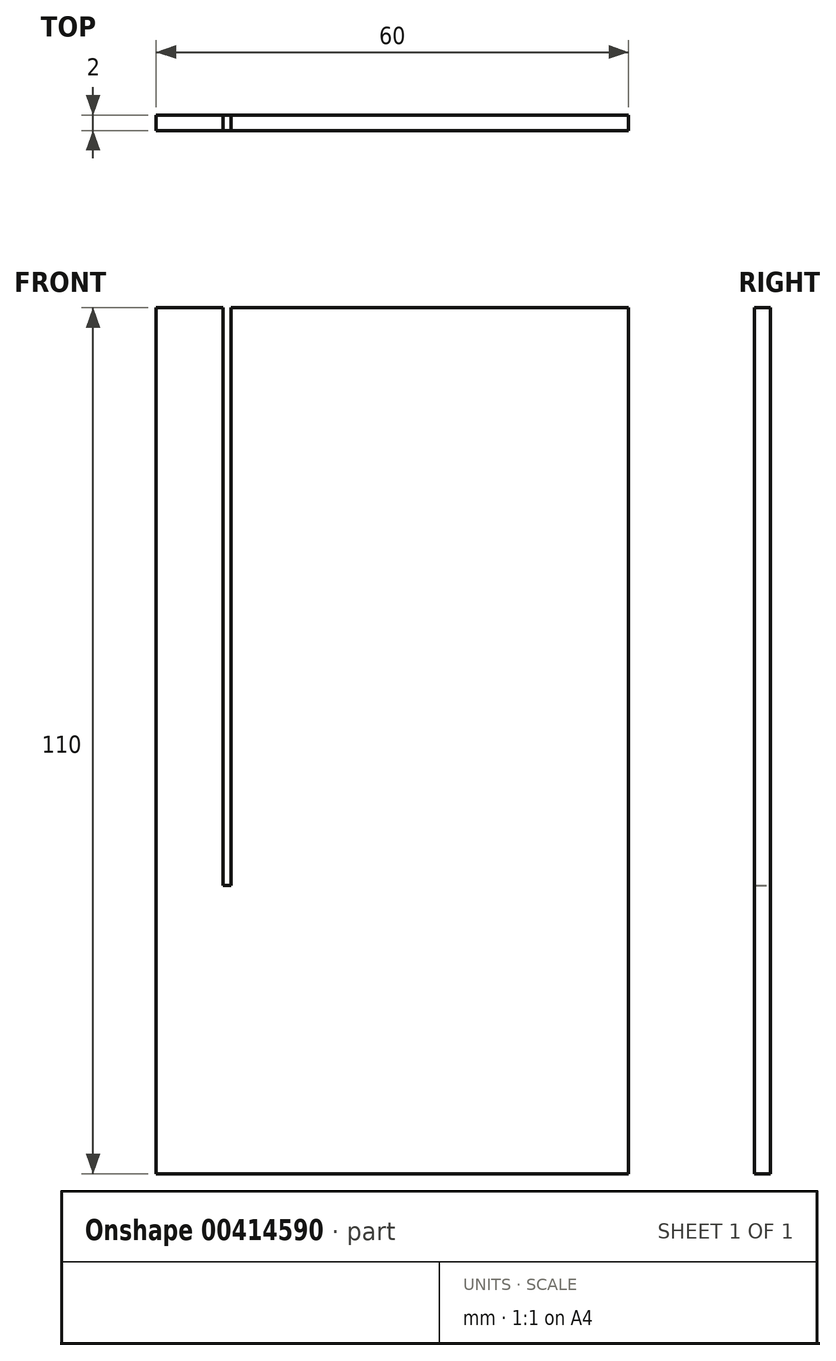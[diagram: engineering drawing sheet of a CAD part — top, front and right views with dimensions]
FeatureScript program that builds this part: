
annotation { "Feature Type Name" : "Feature", "Feature Type Description" : "" }
export const myFeature = defineFeature(function(context is Context, id is Id, definition is map)
    precondition{}
    {
        {
            var Q0;
            Q0=qCreatedBy(makeId("Front.planeOp"),FACE);
            var sketch = newSketch(context, id + "F0", { "sketchPlane" : qUnion([Q0])});
            skLineSegment(sketch, "E0.bottom", {"start": v(-66.46, 57.72) * mm, "end": v(-6.46, 57.72) * mm});
            skLineSegment(sketch, "E0.top", {"start": v(-66.46, -52.28) * mm, "end": v(-6.46, -52.28) * mm});
            skLineSegment(sketch, "E0.left", {"start": v(-66.46, 57.72) * mm, "end": v(-66.46, -52.28) * mm});
            skLineSegment(sketch, "E0.right", {"start": v(-6.46, 57.72) * mm, "end": v(-6.46, -52.28) * mm});
            skLineSegment(sketch, "E1.0", {"start": v(-68.96, 60.22) * mm, "end": v(-68.96, -54.78) * mm});
            skLineSegment(sketch, "E1.1", {"start": v(-68.96, 60.22) * mm, "end": v(-3.96, 60.22) * mm});
            skLineSegment(sketch, "E1.2", {"start": v(-3.96, 60.22) * mm, "end": v(-3.96, -54.78) * mm});
            skLineSegment(sketch, "E1.3", {"start": v(-68.96, -54.78) * mm, "end": v(-3.96, -54.78) * mm});
            skLineSegment(sketch, "E2", {"start": v(-57.96, 57.72) * mm, "end": v(-57.96, -15.68) * mm});
            skLineSegment(sketch, "E3.0", {"start": v(-56.96, 57.72) * mm, "end": v(-56.96, -15.68) * mm});
            skLineSegment(sketch, "E4", {"start": v(-57.96, -15.68) * mm, "end": v(-56.96, -15.68) * mm});
            skLineSegment(sketch, "E5", {"start": v(-66.46, 57.72) * mm, "end": v(-66.46, 60.22) * mm});
            skLineSegment(sketch, "E6", {"start": v(-57.96, 57.72) * mm, "end": v(-57.96, 60.22) * mm});
            skSolve(sketch);
        }
        {
            var Q0;
            Q0=makeQuery(id+"F0.imprint","IMPRINT",FACE,{"disambiguationData":[TD([[makeQuery(id+"F0.imprint","IMPRINT",EDGE,{"derivedFrom":sQuery(id+"F0.wireOp",EDGE,"E0.top")}),1.0]])]});
            extrude(context, id + "F1", {"entities" : qUnion([Q0]), "depth" : 2 * mm});
        }
    });
